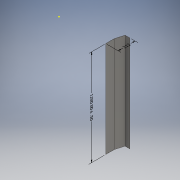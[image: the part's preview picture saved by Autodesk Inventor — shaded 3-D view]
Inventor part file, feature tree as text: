
AUTODESK INVENTOR PART (.ipt)
format: ipt  version: 2018 (Build 220112000, 112)  size: 121,856 bytes
history: native  units: mm
features: other x6, sketch x3, reference x2, extrude x1
ambient origin geometry x8: Origin, YZ Plane, XZ Plane, XY Plane, X Axis, Y Axis, Z Axis, Center Point
bodies: Solid1 (feature_tree)
feature tree (12):
  other  "Annotations"
  sketch  "Sketch1"  dims[d3=1200.0mm d4=0.0mm d5=1200.0mm d6=212.068144mm]
  extrude  "Extrusion1"  Depth=1200.0mm
  sketch  "Sketch3"
  reference  "Reference1"
  reference  "Reference2"
  sketch  "Sketch2"
  other  "Lathe Model 2018.iam"
  other  "Right Leg:1"
  other  "polycarbonate cover:1"
  other  "Linear Dimension 1"
  other  "Linear Dimension 2"
